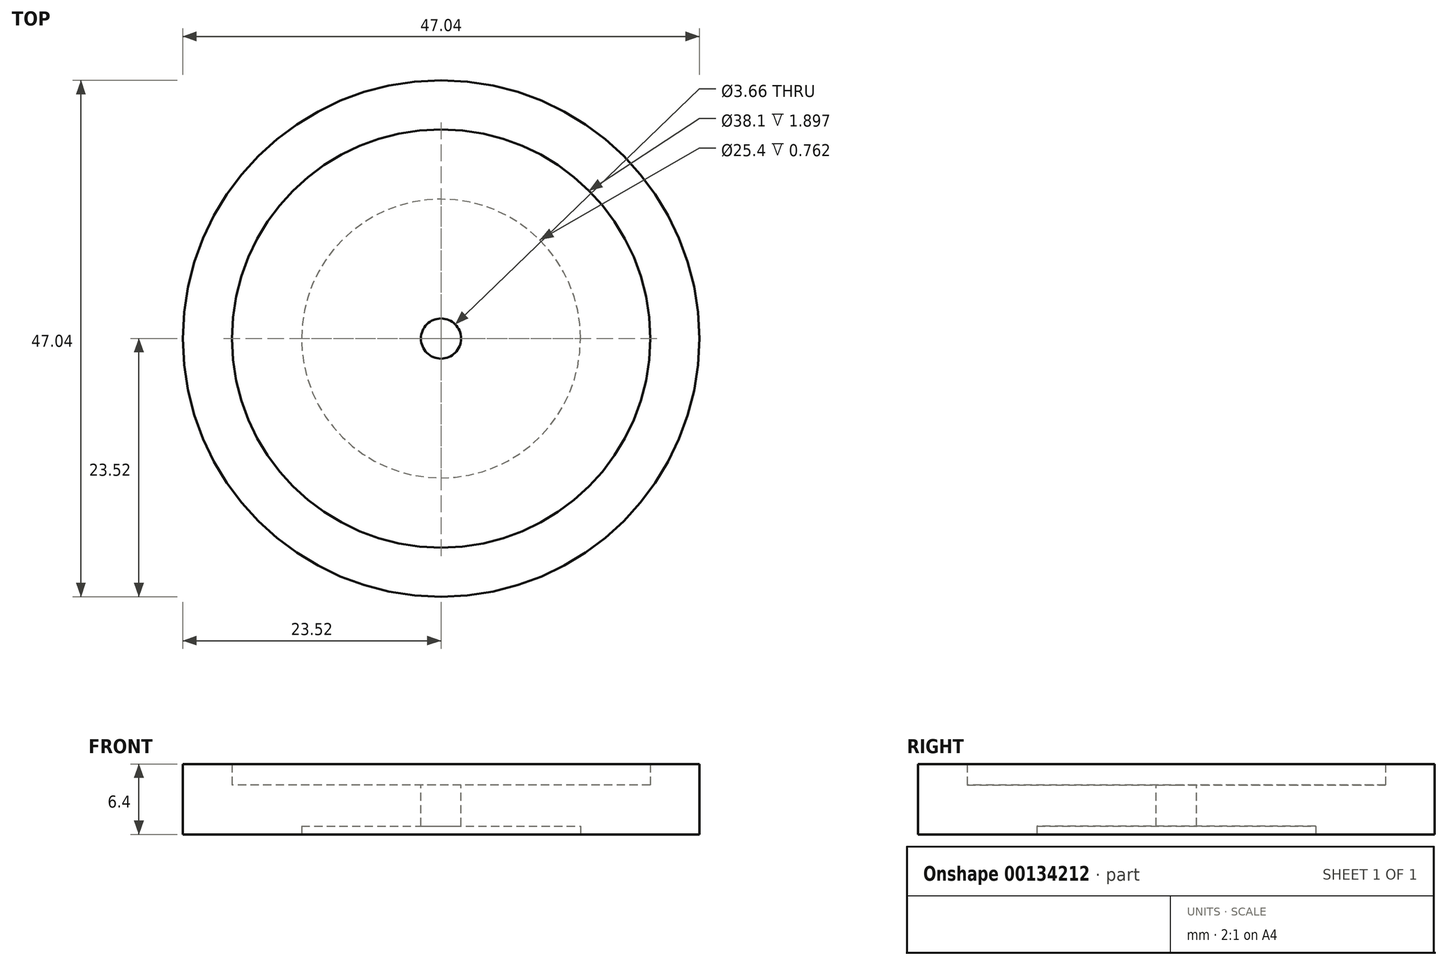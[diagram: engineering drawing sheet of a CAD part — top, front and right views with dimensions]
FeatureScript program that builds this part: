
annotation { "Feature Type Name" : "Feature", "Feature Type Description" : "" }
export const myFeature = defineFeature(function(context is Context, id is Id, definition is map)
    precondition{}
    {
        {
            var Q0;
            Q0=qCreatedBy(makeId("Top.planeOp"),FACE);
            var sketch = newSketch(context, id + "F0", { "sketchPlane" : qUnion([Q0])});
            skCircle(sketch, "E0", {"center": v(0, 0) * mm, "radius": 23.52 * mm});
            skCircle(sketch, "E1", {"center": v(0, 0) * mm, "radius": 19.05 * mm});
            skSolve(sketch);
        }
        {
            var Q0;
            Q0=makeQuery(id+"F0.imprint","IMPRINT",FACE,{"disambiguationData":[TD([[makeQuery(id+"F0.imprint","IMPRINT",EDGE,{"derivedFrom":sQuery(id+"F0.wireOp",EDGE,"E0")}),1.0]])]});
            extrude(context, id + "F1", {"entities" : qUnion([Q0]), "depth" : 6.4 * mm});
        }
        {
            var Q0;
            Q0=makeQuery(id+"F0.imprint","IMPRINT",FACE,{"disambiguationData":[TD([[makeQuery(id+"F0.imprint","IMPRINT",EDGE,{"derivedFrom":sQuery(id+"F0.wireOp",EDGE,"E1")}),1.0]])]});
            extrude(context, id + "F2", {"entities" : qUnion([Q0]), "operationType" : NewBodyOperationType.ADD, "depth" : (7 - (0.4 + 0.79) - 1.3 - 0) * mm});
        }
        {
            var Q0;
            Q0=makeQuery(id+"F2.opExtrude","CAP_FACE",FACE,{"disambiguationData":[OSD([sQuery(id+"F0.wireOp",EDGE,"E1")])],"isStart":false});
            var sketch = newSketch(context, id + "F3", { "sketchPlane" : qUnion([Q0])});
            skPoint(sketch, "E2", {"position": v(0, 0) * mm});
            skSolve(sketch);
        }
        {
            var Q0;
            Q0=sQuery(id+"F3.wireOp",VERTEX,"E2");
            var Q1;
            Q1=makeQuery(id+"F1.opExtrude","SWEPT_BODY",BODY,{"disambiguationData":[OSD([sQuery(id+"F0.wireOp",EDGE,"E0"),sQuery(id+"F0.wireOp",EDGE,"E1")])]});
            hole(context, id + "F4", {"style" : HoleStyle.SIMPLE, "endStyle" : HoleEndStyle.BLIND, "standardTappedOrClearance" : lookupTablePath({ "standard" : "ANSI", "engagement" : "50%", "pitch" : "32 tpi", "size" : "#8", "type" : "Tapped" }), "standardBlindInLast" : lookupTablePath({ "standard" : "ANSI", "engagement" : "50%", "pitch" : "32 tpi", "size" : "#8", "type" : "Tapped" }), "holeDiameter" : 3.66 * mm, "holeDepth" : 12.7 * mm, "startFromSketch" : true, "locations" : qUnion([Q0]), "scope" : qUnion([Q1]), "majorDiameter" : 4.17 * mm});
        }
        {
            var Q0;
            {var subQ0=sQuery(id+"F0.wireOp",EDGE,"E1");Q0=makeQuery(id+"F2.boolean.opBoolean","MERGE",FACE,{"derivedFrom":[makeQuery(id+"F1.opExtrude","CAP_FACE",FACE,{"disambiguationData":[OSD([sQuery(id+"F0.wireOp",EDGE,"E0"),subQ0])],"isStart":true}),makeQuery(id+"F2.opExtrude","CAP_FACE",FACE,{"disambiguationData":[OSD([subQ0])],"isStart":true})]});}
            var sketch = newSketch(context, id + "F5", { "sketchPlane" : qUnion([Q0])});
            skCircle(sketch, "E3", {"center": v(0, 0) * mm, "radius": 12.7 * mm});
            skSolve(sketch);
        }
        {
            var Q0;
            Q0 = qSketchRegion(id + "F5", true);
            extrude(context, id + "F6", {"entities" : qUnion([Q0]), "operationType" : NewBodyOperationType.REMOVE, "oppositeDirection" : true, "depth" : 0.76 * mm});
        }
    });
